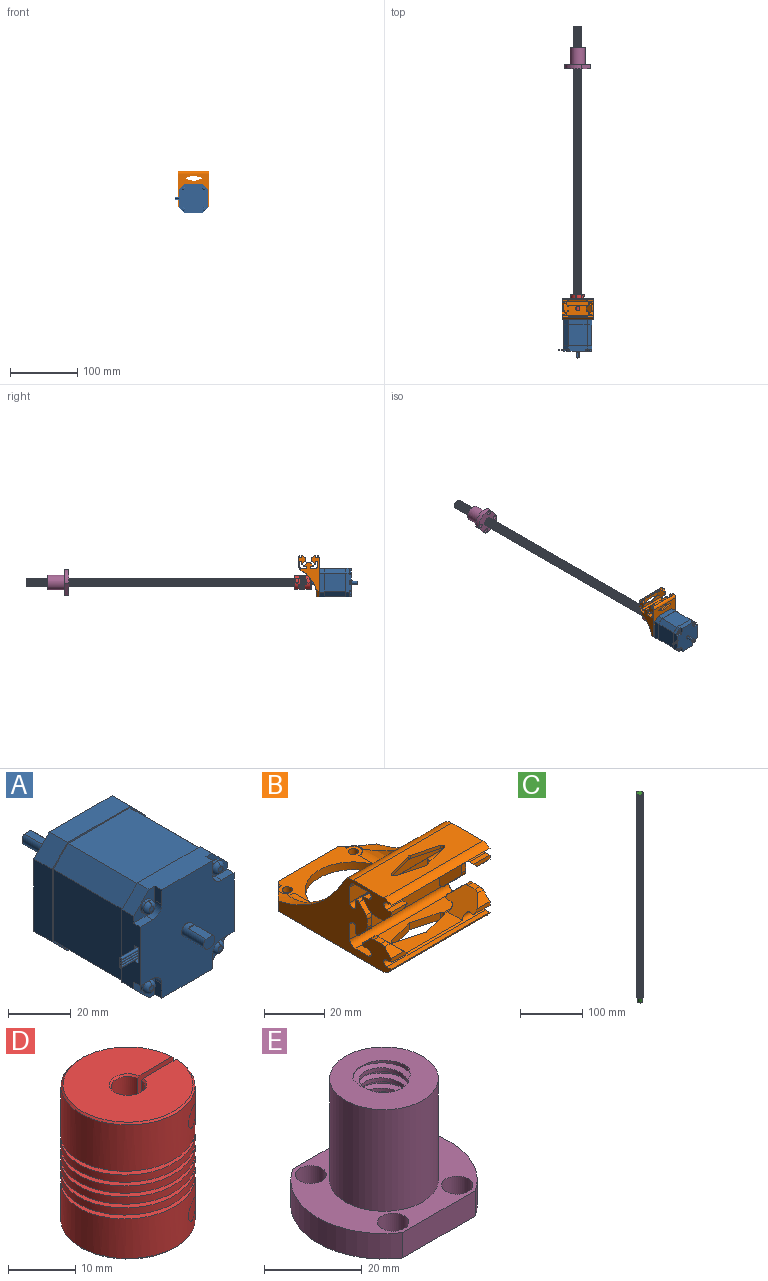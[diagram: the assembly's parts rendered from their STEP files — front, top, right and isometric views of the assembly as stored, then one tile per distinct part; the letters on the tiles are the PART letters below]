
ASSEMBLY  parts=5 mates=4
PART A: 93 faces, bbox 49.3x82x42.3 mm
  f0: plane 42.3x42.3mm, normal (0,1,0), area 858.8mm2, adj f1,f13,f15,f17,f19,f21,f32,f34
  f1: plane 8.25x7mm, normal (0.71,0,0.71), area 81.7mm2, adj f0,f3,f21,f34
  f2: plane 7x7mm, normal (0.71,0,0.71), area 52mm2, adj f12,f22,f23,f35
  f3: plane 42.3x42.3mm, normal (0,-1,0), area 75.6mm2, adj f1,f4,f5,f6,f7,f8,f9,f10
  f4: plane 31.5x6.71mm, normal (0.71,0,0.71), area 298.8mm2, adj f3,f5,f11,f12
  f5: plane 31.5x27.89mm, normal (1,0,0), area 878.4mm2, adj f3,f4,f6,f12
  f6: plane 31.5x6.71mm, normal (0.71,0,-0.71), area 298.8mm2, adj f3,f5,f7,f12
  f7: plane 31.5x27.89mm, normal (0,0,-1), area 878.4mm2, adj f3,f6,f8,f12
  f8: plane 31.5x6.71mm, normal (-0.71,0,-0.71), area 298.8mm2, adj f3,f7,f9,f12
  f9: plane 31.5x27.89mm, normal (-1,0,0), area 878.4mm2, adj f3,f8,f10,f12
  f10: plane 31.5x6.71mm, normal (-0.71,0,0.71), area 298.8mm2, adj f3,f9,f11,f12
  f11: plane 31.5x27.89mm, normal (0,0,1), area 878.4mm2, adj f3,f4,f10,f12
  f12: plane 42.3x42.3mm, normal (0,1,0), area 75.6mm2, adj f2,f4,f5,f6,f7,f8,f9,f10
  f13: plane 28.3x8.25mm, normal (-1,0,0), area 233.5mm2, adj f0,f3,f15,f32
  f14: plane 28.3x8.25mm, normal (-1,0,0), area 207.1mm2, adj f12,f16,f27,f29,f31,f33,f49,f50
  f15: plane 8.25x7mm, normal (-0.71,0,-0.71), area 81.7mm2, adj f0,f3,f13,f17
  f16: plane 7x7mm, normal (-0.71,0,-0.71), area 52mm2, adj f12,f14,f18,f49
  f17: plane 28.3x8.25mm, normal (0,0,-1), area 233.5mm2, adj f0,f3,f15,f19
  f18: plane 28.3x8.25mm, normal (0,0,-1), area 217.6mm2, adj f12,f16,f20,f27,f41,f42,f48,f49
  f19: plane 8.25x7mm, normal (0.71,0,-0.71), area 81.7mm2, adj f0,f3,f17,f21
  f20: plane 7x7mm, normal (0.71,0,-0.71), area 52mm2, adj f12,f18,f22,f41
  f21: plane 28.3x8.25mm, normal (1,0,0), area 233.5mm2, adj f0,f1,f3,f19
  f22: plane 28.3x8.25mm, normal (1,0,0), area 217.6mm2, adj f2,f12,f20,f23,f26,f27,f40,f41
  f23: plane 9.65x9.65mm, normal (0,-1,0), area 46.4mm2, adj f2,f22,f24,f25,f26,f35,f60
  f24: plane 5.65x3mm, normal (1,0,0), area 17mm2, adj f23,f25,f27,f35
  f25: cylinder r=4mm len=4mm, axis (0,1,0), area 18.8mm2, adj f23,f24,f26,f27
  f26: plane 5.65x3mm, normal (0,0,1), area 17mm2, adj f22,f23,f25,f27
  f27: plane 42.3x42.3mm, normal (0,-1,0), area 1410.9mm2, adj f14,f18,f22,f24,f25,f26,f28,f30
  f28: plane 5.65x3mm, normal (-1,0,0), area 17mm2, adj f27,f29,f30,f35
  f29: plane 9.65x9.65mm, normal (0,-1,0), area 46.4mm2, adj f14,f28,f30,f31,f33,f35,f36
  f30: cylinder r=4mm len=4mm, axis (0,-1,0), area 18.8mm2, adj f27,f28,f29,f31
  f31: plane 5.65x3mm, normal (0,0,1), area 17mm2, adj f14,f27,f29,f30
  f32: plane 8.25x7mm, normal (-0.71,0,0.71), area 81.7mm2, adj f0,f3,f13,f34
  f33: plane 7x7mm, normal (-0.71,0,0.71), area 52mm2, adj f12,f14,f29,f35
  f34: plane 28.3x8.25mm, normal (0,0,1), area 233.5mm2, adj f0,f1,f3,f32
  f35: plane 28.3x8.25mm, normal (0,0,1), area 217.6mm2, adj f2,f12,f23,f24,f27,f28,f29,f33
  f36: cylinder r=2.45mm len=4.9mm, axis (0,-1,0), area 15.4mm2, adj f29,f37,f39
  f37: torus R=0.95mm, axis (0,-1,0), area 14.1mm2, adj f36,f38,f39
  f38: plane 1.9x1.9mm, normal (0,-1,0), area 2.8mm2, adj f37,f39
  f39: torus R=0.95mm, axis (0,-1,0), area 14.1mm2, adj f36,f37,f38
  f40: plane 5.65x3mm, normal (0,0,-1), area 17mm2, adj f22,f27,f41,f43
  f41: plane 9.65x9.65mm, normal (0,-1,0), area 46.4mm2, adj f18,f20,f22,f40,f42,f43,f44
  f42: plane 5.65x3mm, normal (1,0,0), area 17mm2, adj f18,f27,f41,f43
  f43: cylinder r=4mm len=4mm, axis (0,-1,0), area 18.8mm2, adj f27,f40,f41,f42
  f44: cylinder r=2.45mm len=4.9mm, axis (0,-1,0), area 15.4mm2, adj f41,f45,f47
  f45: torus R=0.95mm, axis (0,-1,0), area 14.1mm2, adj f44,f46,f47
  f46: plane 1.9x1.9mm, normal (0,-1,0), area 2.8mm2, adj f45,f47
  f47: torus R=0.95mm, axis (0,-1,0), area 14.1mm2, adj f44,f45,f46
  f48: plane 5.65x3mm, normal (-1,0,0), area 17mm2, adj f18,f27,f49,f51
  f49: plane 9.65x9.65mm, normal (0,-1,0), area 46.4mm2, adj f14,f16,f18,f48,f50,f51,f52
  f50: plane 5.65x3mm, normal (0,0,-1), area 17mm2, adj f14,f27,f49,f51
  f51: cylinder r=4mm len=4mm, axis (0,1,0), area 18.8mm2, adj f27,f48,f49,f50
  f52: cylinder r=2.45mm len=4.9mm, axis (0,1,0), area 15.4mm2, adj f49,f53,f55
  f53: torus R=0.95mm, axis (0,1,0), area 14.1mm2, adj f52,f54,f55
  f54: plane 1.9x1.9mm, normal (0,-1,0), area 2.8mm2, adj f53,f55
  f55: torus R=0.95mm, axis (0,1,0), area 14.1mm2, adj f52,f53,f54
  f56: cylinder r=2.5mm len=10mm, axis (0,-1,0), area 131.3mm2, adj f27,f57,f58,f59
  f57: plane 8x3mm, normal (0,0,1), area 24mm2, adj f56,f58,f59
  f58: plane 5x4.5mm, normal (0,-1,0), area 18.6mm2, adj f56,f57
  f59: plane 3x0.5mm, normal (0,-1,0), area 1mm2, adj f56,f57
  f60: cylinder r=2.45mm len=4.9mm, axis (0,1,0), area 15.4mm2, adj f23,f61,f63
  f61: torus R=0.95mm, axis (0,1,0), area 14.1mm2, adj f60,f62,f63
  f62: plane 1.9x1.9mm, normal (0,-1,0), area 2.8mm2, adj f61,f63
  f63: torus R=0.95mm, axis (0,1,0), area 14.1mm2, adj f60,f61,f62
  f64: plane 3x1.75mm, normal (0,0,1), area 5.3mm2, adj f14,f65,f67,f68
  f65: plane 6x3mm, normal (0,-1,0), area 18mm2, adj f14,f64,f66,f68
  f66: plane 3x1.75mm, normal (0,0,-1), area 5.3mm2, adj f14,f65,f67,f68
  f67: plane 6x3mm, normal (0,1,0), area 18mm2, adj f14,f64,f66,f68
  f68: plane 6x1.75mm, normal (-1,0,0), area 7.6mm2, adj f64,f65,f66,f67,f69,f71,f73,f75
  f69: cylinder r=0.48mm len=10mm, axis (-1,0,0), area 30mm2, adj f68,f70
  f70: plane 0.96x0.96mm, normal (-1,0,0), area 0.7mm2, adj f69
  f71: cylinder r=0.48mm len=10mm, axis (-1,0,0), area 30mm2, adj f68,f72
  f72: plane 0.96x0.96mm, normal (-1,0,0), area 0.7mm2, adj f71
  f73: cylinder r=0.48mm len=10mm, axis (-1,0,0), area 30mm2, adj f68,f74
  f74: plane 0.96x0.96mm, normal (-1,0,0), area 0.7mm2, adj f73
  f75: cylinder r=0.48mm len=10mm, axis (-1,0,0), area 30mm2, adj f68,f76
  f76: plane 0.96x0.96mm, normal (-1,0,0), area 0.7mm2, adj f75
  f77: cylinder r=1.5mm len=4.5mm, axis (0,-1,0), area 42.4mm2, adj f0,f78
  f78: plane 3x3mm, normal (0,1,0), area 7.1mm2, adj f77
  f79: cylinder r=1.5mm len=4.5mm, axis (0,1,0), area 42.4mm2, adj f0,f80
  f80: plane 3x3mm, normal (0,1,0), area 7.1mm2, adj f79
  f81: cylinder r=1.5mm len=4.5mm, axis (0,1,0), area 42.4mm2, adj f0,f82
  f82: plane 3x3mm, normal (0,1,0), area 7.1mm2, adj f81
  f83: cylinder r=1.5mm len=4.5mm, axis (0,-1,0), area 42.4mm2, adj f0,f84
  f84: plane 3x3mm, normal (0,1,0), area 7.1mm2, adj f83
  f85: cylinder r=16mm len=32mm, axis (0,1,0), area 40.2mm2, adj f0,f86
  f86: plane 32x32mm, normal (0,1,0), area 424.1mm2, adj f85,f87
  f87: cylinder r=11mm len=22mm, axis (0,1,0), area 165.9mm2, adj f86,f88
  f88: plane 22x22mm, normal (0,1,0), area 360.5mm2, adj f87,f89
  f89: cylinder r=2.5mm len=22mm, axis (0,1,0), area 297.3mm2, adj f88,f90,f91,f92
  f90: plane 3x0.5mm, normal (0,1,0), area 1mm2, adj f89,f91
  f91: plane 15x3mm, normal (0,0,1), area 45mm2, adj f89,f90,f92
  f92: plane 5x4.5mm, normal (0,1,0), area 18.6mm2, adj f89,f91
PART B: 135 faces, bbox 47.1x62.8x30.9 mm
  f0: cylinder r=1.4mm len=11.38mm, axis (1,0,0), area 40.8mm2, adj f41,f57,f59,f110,f115,f127
  f1: cylinder r=1.4mm len=11.38mm, axis (1,0,0), area 40.8mm2, adj f41,f75,f77,f107,f114,f130
  f2: plane 7.5x1.61mm, normal (0,-1,0), area 10.7mm2, adj f41,f83,f84,f114
  f3: plane 7.5x1.61mm, normal (0,-1,0), area 10.7mm2, adj f41,f50,f51,f115
  f4: plane 7.5x2.03mm, normal (0,0,1), area 15.2mm2, adj f38,f43,f49,f111
  f5: plane 5.89x3.16mm, normal (0,-0.71,-0.71), area 19.3mm2, adj f6,f38,f43,f111
  f6: cylinder r=2.75mm len=2.73mm, axis (1,0,0), area 4.2mm2, adj f5,f7,f38,f111
  f7: plane 3.24x2.22mm, normal (0,0,-1), area 7.2mm2, adj f6,f8,f38,f111
  f8: cylinder r=2.75mm len=2.73mm, axis (1,0,0), area 4.2mm2, adj f7,f9,f38,f111
  f9: plane 6.06x3.33mm, normal (0,0.71,-0.71), area 20.7mm2, adj f8,f10,f38,f111
  f10: cylinder r=0.72mm len=7.5mm, axis (1,0,0), area 14.9mm2, adj f9,f11,f38,f111
  f11: plane 7.5x2.14mm, normal (0,0,1), area 16mm2, adj f10,f38,f58,f111
  f12: plane 7.2x2.13mm, normal (0,1,0), area 15.3mm2, adj f13,f38,f62,f112
  f13: cylinder r=0.72mm len=7.2mm, axis (1,0,0), area 14.3mm2, adj f12,f14,f38,f112
  f14: plane 5.76x3.33mm, normal (0,-0.71,0.71), area 19.3mm2, adj f13,f15,f38,f112
  f15: cylinder r=2.75mm len=2.43mm, axis (1,0,0), area 3.6mm2, adj f14,f16,f38,f108,f112
  f16: plane 3.24x2mm, normal (0,-1,0), area 6.5mm2, adj f15,f17,f38,f108
  f17: cylinder r=2.75mm len=3.09mm, axis (1,0,0), area 6.3mm2, adj f16,f18,f38,f108,f112
  f18: plane 5.76x2.67mm, normal (0,-0.71,-0.71), area 16.7mm2, adj f17,f19,f38,f112
  f19: cylinder r=0.72mm len=7.2mm, axis (1,0,0), area 14.3mm2, adj f18,f20,f38,f112
  f20: plane 7.2x2.13mm, normal (0,1,0), area 15.3mm2, adj f19,f21,f38,f112
  f21: cylinder r=1.4mm len=10mm, axis (1,0,0), area 37.8mm2, adj f20,f38,f73,f112
  f22: plane 7.5x2.13mm, normal (0,0,-1), area 16mm2, adj f23,f38,f76,f113
  f23: cylinder r=0.72mm len=7.5mm, axis (1,0,0), area 14.9mm2, adj f22,f24,f38,f113
  f24: plane 6.06x3.33mm, normal (0,0.71,0.71), area 20.7mm2, adj f23,f25,f38,f113
  f25: cylinder r=2.75mm len=2.73mm, axis (1,0,0), area 4.2mm2, adj f24,f26,f38,f113
  f26: plane 3.24x2.22mm, normal (0,0,1), area 7.2mm2, adj f25,f27,f38,f113
  f27: cylinder r=2.75mm len=2.73mm, axis (1,0,0), area 4.2mm2, adj f26,f28,f38,f113
  f28: plane 5.89x3.16mm, normal (0,-0.71,0.71), area 19.3mm2, adj f27,f38,f42,f113
  f29: plane 7.5x2.03mm, normal (0,0,-1), area 15.2mm2, adj f38,f42,f85,f113
  f30: cylinder r=1.7mm len=3.4mm, axis (0,0,-1), area 33.9mm2, adj f37,f46
  f31: cylinder r=1.7mm len=3.4mm, axis (0,0,-1), area 33.9mm2, adj f34,f46
  f32: cylinder r=1.7mm len=3.4mm, axis (0,0,-1), area 33.9mm2, adj f40,f46
  f33: cylinder r=1.7mm len=3.4mm, axis (0,0,-1), area 33.9mm2, adj f40,f46
  f34: plane 13.35x12.54mm, normal (0,0,1), area 46.3mm2, adj f31,f35,f45,f98,f103
  f35: cylinder r=6mm len=28.38mm, axis (0,1,0), area 205.2mm2, adj f34,f40,f45,f87,f90,f99,f103,f105
  f36: cylinder r=6mm len=1.74mm, axis (0,-1,0), area 1.1mm2, adj f40,f89,f106,f133
  f37: plane 13.35x12.54mm, normal (0,0,1), area 46.3mm2, adj f30,f45,f91,f96,f104
  f38: plane 53x30.18mm, normal (1,0,0), area 754.6mm2, adj f4,f5,f6,f7,f8,f9,f10,f11
  f39: plane 30.3x21.02mm, normal (0,1,0), area 601.9mm2, adj f92,f94,f96,f97,f98,f100,f117
  f40: plane 37x16mm, normal (0,0,1), area 257.9mm2, adj f32,f33,f35,f36,f44,f45,f91,f93
  f41: plane 53x30.18mm, normal (-1,0,0), area 754.6mm2, adj f0,f1,f2,f3,f46,f47,f48,f49
  f42: plane 7.5x1.61mm, normal (0,-1,0), area 10.7mm2, adj f28,f29,f38,f113
  f43: plane 7.5x1.61mm, normal (0,-1,0), area 10.7mm2, adj f4,f5,f38,f111
  f44: plane 28.3x3.18mm, normal (0,1,0), area 89.9mm2, adj f40,f46,f133,f134
  f45: cylinder r=16mm len=32mm, axis (0,0,-1), area 319.2mm2, adj f34,f35,f37,f40,f46,f91,f97
  f46: plane 57.47x46.3mm, normal (0,0,-1), area 1624.3mm2, adj f30,f31,f32,f33,f38,f41,f44,f45
  f47: plane 46.3x14.48mm, normal (0,0,1), area 555.3mm2, adj f38,f41,f100,f101,f118,f119,f120,f121
  f48: plane 46.3x2.03mm, normal (0,0,-1), area 93.8mm2, adj f38,f41,f49,f101
  f49: cylinder r=1.4mm len=46.3mm, axis (1,0,0), area 103.6mm2, adj f4,f38,f41,f48,f50,f110,f111,f115
  f50: plane 7.5x2.03mm, normal (0,0,1), area 15.2mm2, adj f3,f41,f49,f115
  f51: plane 5.89x3.16mm, normal (0,-0.71,-0.71), area 19.3mm2, adj f3,f41,f52,f115
  f52: cylinder r=2.75mm len=2.73mm, axis (1,0,0), area 4.2mm2, adj f41,f51,f53,f115
  f53: plane 3.24x2.22mm, normal (0,0,-1), area 7.2mm2, adj f41,f52,f54,f115
  f54: cylinder r=2.75mm len=2.73mm, axis (1,0,0), area 4.2mm2, adj f41,f53,f55,f115
  f55: plane 6.06x3.33mm, normal (0,0.71,-0.71), area 20.7mm2, adj f41,f54,f56,f115
  f56: cylinder r=0.72mm len=7.5mm, axis (1,0,0), area 14.9mm2, adj f41,f55,f57,f115
  f57: plane 7.5x2.14mm, normal (0,0,1), area 16mm2, adj f0,f41,f56,f115
  f58: cylinder r=1.4mm len=11.38mm, axis (1,0,0), area 40.8mm2, adj f11,f38,f59,f110,f111,f128
  f59: plane 46.3x6.22mm, normal (0,0,-1), area 233.1mm2, adj f0,f38,f41,f58,f60,f120,f121,f126
  f60: cylinder r=2.4mm len=46.3mm, axis (1,0,0), area 177.1mm2, adj f38,f41,f59,f61
  f61: plane 46.3x6.22mm, normal (0,-1,0), area 288.1mm2, adj f38,f41,f60,f62
  f62: cylinder r=1.4mm len=46.3mm, axis (1,0,0), area 77.7mm2, adj f12,f38,f41,f61,f63,f73,f112,f116
  f63: plane 7.2x2.13mm, normal (0,1,0), area 15.3mm2, adj f41,f62,f64,f116
  f64: cylinder r=0.72mm len=7.2mm, axis (1,0,0), area 14.3mm2, adj f41,f63,f65,f116
  f65: plane 5.76x3.33mm, normal (0,-0.71,0.71), area 19.3mm2, adj f41,f64,f66,f116
  f66: cylinder r=2.75mm len=2.43mm, axis (1,0,0), area 3.6mm2, adj f41,f65,f67,f109,f116
  f67: plane 3.24x2mm, normal (0,-1,0), area 6.5mm2, adj f41,f66,f68,f109
  f68: cylinder r=2.75mm len=3.09mm, axis (1,0,0), area 6.3mm2, adj f41,f67,f69,f109,f116
  f69: plane 5.76x2.67mm, normal (0,-0.71,-0.71), area 16.7mm2, adj f41,f68,f70,f116
  f70: cylinder r=0.72mm len=7.2mm, axis (1,0,0), area 14.3mm2, adj f41,f69,f71,f116
  f71: plane 7.2x2.13mm, normal (0,1,0), area 15.3mm2, adj f41,f70,f72,f116
  f72: cylinder r=1.4mm len=10mm, axis (1,0,0), area 37.8mm2, adj f41,f71,f73,f116
  f73: plane 46.3x14.87mm, normal (0,-1,0), area 483.8mm2, adj f21,f38,f41,f62,f72,f74,f112,f116
  f74: cylinder r=2.4mm len=46.3mm, axis (1,0,0), area 177.1mm2, adj f38,f41,f73,f75
  f75: plane 46.3x6.22mm, normal (0,0,1), area 233.1mm2, adj f1,f38,f41,f74,f76,f122,f123,f130
  f76: cylinder r=1.4mm len=11.38mm, axis (1,0,0), area 40.8mm2, adj f22,f38,f75,f107,f113,f132
  f77: plane 7.5x2.13mm, normal (0,0,-1), area 16mm2, adj f1,f41,f78,f114
  f78: cylinder r=0.72mm len=7.5mm, axis (1,0,0), area 14.9mm2, adj f41,f77,f79,f114
  f79: plane 6.06x3.33mm, normal (0,0.71,0.71), area 20.7mm2, adj f41,f78,f80,f114
  f80: cylinder r=2.75mm len=2.73mm, axis (1,0,0), area 4.2mm2, adj f41,f79,f81,f114
  f81: plane 3.24x2.22mm, normal (0,0,1), area 7.2mm2, adj f41,f80,f82,f114
  f82: cylinder r=2.75mm len=2.73mm, axis (1,0,0), area 4.2mm2, adj f41,f81,f83,f114
  f83: plane 5.89x3.16mm, normal (0,-0.71,0.71), area 19.3mm2, adj f2,f41,f82,f114
  f84: plane 7.5x2.03mm, normal (0,0,-1), area 15.2mm2, adj f2,f41,f85,f114
  f85: cylinder r=1.4mm len=46.3mm, axis (1,0,0), area 103.6mm2, adj f29,f38,f41,f84,f86,f107,f113,f114
  f86: plane 46.3x2.03mm, normal (0,0,1), area 93.8mm2, adj f38,f41,f85,f102
  f87: plane 12.79x11.02mm, normal (1,0,0), area 61.5mm2, adj f35,f90,f94
  f88: plane 12.79x11.02mm, normal (-1,0,0), area 61.5mm2, adj f89,f91,f92
  f89: cylinder r=45mm len=38.01mm, axis (1,0,0), area 113.1mm2, adj f36,f38,f88,f91,f92,f100,f106,f133
  f90: cylinder r=45mm len=38.01mm, axis (1,0,0), area 113.1mm2, adj f35,f41,f87,f93,f94,f100,f105,f134
  f91: cylinder r=6mm len=28.38mm, axis (0,-1,0), area 205.2mm2, adj f37,f40,f45,f88,f89,f95,f104,f106
  f92: cylinder r=6mm len=20.88mm, axis (0,0,-1), area 160.6mm2, adj f39,f88,f89,f95,f100
  f93: cylinder r=6mm len=1.74mm, axis (0,1,0), area 1.1mm2, adj f40,f90,f105,f134
  f94: cylinder r=6mm len=20.88mm, axis (0,0,1), area 160.6mm2, adj f39,f87,f90,f99,f100
  f95: bspline ~7.42x6mm, area 34.4mm2, adj f91,f92,f96,f104
  f96: cylinder r=5mm len=9.19mm, axis (-1,0,0), area 67mm2, adj f37,f39,f95,f97,f104
  f97: bspline ~14.98x5.95mm, area 84.3mm2, adj f39,f45,f96,f98
  f98: cylinder r=5mm len=9.19mm, axis (-1,0,0), area 67mm2, adj f34,f39,f97,f99,f103
  f99: bspline ~6.36x6mm, area 34.4mm2, adj f35,f94,f98,f103
  f100: cylinder r=5mm len=46.3mm, axis (1,0,0), area 183.2mm2, adj f38,f39,f41,f47,f89,f90,f92,f94
  f101: cylinder r=5mm len=46.3mm, axis (-1,0,0), area 171.1mm2, adj f38,f41,f47,f48
  f102: cylinder r=5mm len=46.3mm, axis (-1,0,0), area 262.3mm2, adj f38,f41,f46,f86
  f103: cylinder r=3mm len=6mm, axis (0,0,1), area 13.3mm2, adj f34,f35,f98,f99
  f104: cylinder r=3mm len=6mm, axis (0,0,1), area 13.3mm2, adj f37,f91,f95,f96
  f105: cylinder r=3mm len=6mm, axis (0,0,1), area 3.3mm2, adj f35,f40,f90,f93
  f106: cylinder r=3mm len=6mm, axis (0,0,1), area 3.3mm2, adj f36,f40,f89,f91
  f107: plane 26.3x6.97mm, normal (0,0,1), area 143.8mm2, adj f1,f76,f85,f113,f114,f124,f125,f130
  f108: plane 4.5x0.07mm, normal (-1,0,0), area 0.3mm2, adj f15,f16,f17,f112
  f109: plane 4.5x0.07mm, normal (1,0,0), area 0.3mm2, adj f66,f67,f68,f116
  f110: plane 26.3x6.97mm, normal (0,0,-1), area 143.8mm2, adj f0,f49,f58,f111,f115,f118,f119,f127
  f111: plane 14.33x8.54mm, normal (-0.71,0,-0.71), area 99.5mm2, adj f4,f5,f6,f7,f8,f9,f10,f11
  f112: plane 15.01x8.62mm, normal (-0.71,-0.71,0), area 103.6mm2, adj f12,f13,f14,f15,f17,f18,f19,f20
  f113: plane 14.33x8.54mm, normal (-0.71,0,0.71), area 99.5mm2, adj f22,f23,f24,f25,f26,f27,f28,f29
  f114: plane 14.33x8.54mm, normal (0.71,0,0.71), area 99.5mm2, adj f1,f2,f77,f78,f79,f80,f81,f82
  f115: plane 14.33x8.54mm, normal (0.71,0,-0.71), area 99.5mm2, adj f0,f3,f49,f50,f51,f52,f53,f54
  f116: plane 15.01x8.62mm, normal (0.71,-0.71,0), area 103.6mm2, adj f62,f63,f64,f65,f66,f68,f69,f70
  f117: cylinder r=3.17mm len=6.35mm, axis (0,1,0), area 32.6mm2, adj f39,f73
  f118: plane 11.12x2.97mm, normal (-0.26,0.97,0), area 18.4mm2, adj f47,f110,f128,f129
  f119: plane 11.12x2.97mm, normal (0.26,0.97,0), area 18.4mm2, adj f47,f110,f127,f129
  f120: plane 11.12x2.97mm, normal (0.26,-0.97,0), area 15mm2, adj f47,f59,f126,f127
  f121: plane 11.12x2.97mm, normal (-0.26,-0.97,0), area 15mm2, adj f47,f59,f126,f128
  f122: plane 11.38x3.03mm, normal (-0.26,-0.97,0), area 33.9mm2, adj f46,f75,f123,f132
  f123: plane 11.38x3.03mm, normal (0.26,-0.97,0), area 33.9mm2, adj f46,f75,f122,f130
  f124: plane 11.12x3.18mm, normal (0.26,0.97,0), area 36.5mm2, adj f46,f107,f130,f131
  f125: plane 11.12x3.18mm, normal (-0.26,0.97,0), area 36.5mm2, adj f46,f107,f131,f132
  f126: cylinder r=1mm len=1.31mm, axis (0,0,-1), area 0.7mm2, adj f47,f59,f120,f121
  f127: cylinder r=1mm len=1.93mm, axis (0,0,-1), area 3.7mm2, adj f0,f47,f59,f110,f119,f120
  f128: cylinder r=1mm len=1.93mm, axis (0,0,-1), area 3.7mm2, adj f47,f58,f59,f110,f118,f121
  f129: cylinder r=1mm len=1.6mm, axis (0,0,-1), area 0.8mm2, adj f47,f110,f118,f119
  f130: cylinder r=1mm len=3.18mm, axis (0,0,-1), area 7.8mm2, adj f1,f46,f75,f107,f123,f124
  f131: cylinder r=1mm len=3.18mm, axis (0,0,-1), area 1.7mm2, adj f46,f107,f124,f125
  f132: cylinder r=1mm len=3.18mm, axis (0,0,-1), area 7.8mm2, adj f46,f75,f76,f107,f122,f125
  f133: plane 9.04x9.04mm, normal (0.71,0.71,0), area 44.5mm2, adj f36,f38,f40,f44,f46,f89
  f134: plane 9.04x9.04mm, normal (-0.71,0.71,0), area 44.5mm2, adj f40,f41,f44,f46,f90,f93
PART C: 10 faces, bbox 12.7x14.7x410.4 mm
  f0: cylinder r=6.35mm len=400.05mm, axis (0,0,-1), area -4638.8mm2, adj f1,f2,f5,f7,f8,f9
  f1: plane 12.7x12.28mm, normal (0,0,-1), area 64.9mm2, adj f0,f3,f5,f6,f7
  f2: plane 12.7x12.29mm, normal (0,0,1), area 115.2mm2, adj f0,f6,f8,f9
  f3: cylinder r=4mm len=10mm, axis (0,0,1), area 251.3mm2, adj f1,f4
  f4: plane 8x8mm, normal (0,0,-1), area 50.3mm2, adj f3
  f5: plane 1.27x0.8mm, normal (0,-1,0), area 0.8mm2, adj f0,f1,f6,f9
  f6: cylinder r=5.08mm len=400.05mm, axis (0,0,1), area 12611.1mm2, adj f1,f2,f5,f7,f8,f9
  f7: bspline ~399.96x14.66mm, area 7450.8mm2, adj f0,f1,f6,f8
  f8: plane 1.27x0.8mm, normal (0,-1,0), area 0.8mm2, adj f0,f2,f6,f7
  f9: bspline ~399.96x14.66mm, area 7483.9mm2, adj f0,f2,f5,f6
PART D: 32 faces, bbox 24.4x23.3x26.3 mm
  f0: cone r=4mm half-angle=45deg, axis (0,0,-1), area 10.7mm2, adj f1,f2,f3,f4
  f1: plane 9.63x7.31mm, normal (0,-1,0), area 42.2mm2, adj f0,f2,f4,f5,f6,f7,f8
  f2: plane 19.4x19.39mm, normal (0,0,-1), area 232.6mm2, adj f0,f1,f3,f5
  f3: plane 9.58x7.31mm, normal (0,1,0), area 41.9mm2, adj f0,f2,f4,f5,f6,f9,f10
  f4: cylinder r=4mm len=12.2mm, axis (0,0,-1), area 244.1mm2, adj f0,f1,f3,f7,f8,f9,f10,f11
  f5: cone r=10mm half-angle=45deg, axis (0,0,1), area 25.9mm2, adj f1,f2,f3,f6
  f6: cylinder r=10mm len=24.4mm, axis (0,0,1), area 1299.1mm2, adj f1,f3,f5,f7,f10,f11,f12,f14
  f7: bspline ~23.13x22mm, area 1185.7mm2, adj f1,f4,f6,f13,f18,f19
  f8: cylinder r=1.7mm len=5.75mm, axis (0,1,0), area 57.2mm2, adj f1,f4,f20
  f9: cylinder r=1.7mm len=8.99mm, axis (0,1,0), area 82.2mm2, adj f3,f4,f21
  f10: bspline ~23.13x22mm, area 195mm2, adj f3,f4,f6,f11
  f11: plane 6x0.7mm, normal (-1,0,0), area 4.2mm2, adj f4,f6,f10,f12
  f12: bspline ~23.13x22mm, area 1319.3mm2, adj f4,f6,f11,f13,f14,f19
  f13: plane 8x7.24mm, normal (0,0,-1), area 19.9mm2, adj f4,f7,f12,f19
  f14: plane 8.92x8.39mm, normal (0,1,0), area 51.3mm2, adj f6,f12,f15,f19,f22,f23,f24
  f15: cone r=9.7mm half-angle=45deg, axis (0,0,-1), area 25.9mm2, adj f6,f14,f16,f23
  f16: plane 8.85x8.39mm, normal (0,-1,0), area 50.9mm2, adj f6,f15,f17,f19,f22,f23,f25
  f17: bspline ~14.4x11.57mm, area 69.1mm2, adj f6,f16,f18,f19
  f18: plane 7.5x0.7mm, normal (1,0,0), area 5.2mm2, adj f6,f7,f17,f19
  f19: cylinder r=2.5mm len=12.2mm, axis (0,0,1), area 159.1mm2, adj f7,f12,f13,f14,f16,f17,f18,f22
  f20: plane 6x5.85mm, normal (0,1,0), area 19mm2, adj f8,f26,f27
  f21: cylinder r=10mm len=3.4mm, axis (0,0,1), area 10.5mm2, adj f9
  f22: cone r=2.5mm half-angle=45deg, axis (0,0,1), area 6.7mm2, adj f14,f16,f19,f23
  f23: plane 19.4x19.39mm, normal (0,0,1), area 264.7mm2, adj f14,f15,f16,f22
  f24: cylinder r=1.7mm len=8.21mm, axis (0,1,0), area 83.7mm2, adj f14,f28
  f25: cylinder r=1.7mm len=5.75mm, axis (0,1,0), area 61.4mm2, adj f16,f29
  f26: cylinder r=10mm len=6mm, axis (0,0,1), area 30.3mm2, adj f20,f27
  f27: cylinder r=3mm len=6mm, axis (0,1,0), area 32.4mm2, adj f20,f26
  f28: cylinder r=10mm len=3.4mm, axis (0,0,1), area 10.5mm2, adj f24
  f29: plane 6x5.85mm, normal (0,1,0), area 19mm2, adj f25,f30,f31
  f30: cylinder r=10mm len=6mm, axis (0,0,1), area 30.3mm2, adj f29,f31
  f31: cylinder r=3mm len=6mm, axis (0,1,0), area 32.4mm2, adj f29,f30
PART E: 29 faces, bbox 38.4x32.1x32.8 mm
  f0: bspline ~31.23x14.66mm, area 563.7mm2, adj f2,f14,f15,f16,f17,f18,f19,f20
  f1: bspline ~30.39x14.66mm, area 539.1mm2, adj f2,f14,f15,f16,f17,f18,f19,f20
  f2: cylinder r=5.08mm len=30.15mm, axis (0,0,-1), area 304.8mm2, adj f0,f1,f14,f28
  f3: cylinder r=19.05mm len=31.75mm, axis (0,0,-1), area 238.3mm2, adj f4,f10,f11,f12
  f4: plane 21.06x6.35mm, normal (0,1,0), area 133.7mm2, adj f3,f5,f11,f12
  f5: cylinder r=19.05mm len=31.75mm, axis (0,0,-1), area 238.3mm2, adj f4,f10,f11,f12
  f6: cylinder r=3.17mm len=6.35mm, axis (0,0,-1), area 126.7mm2, adj f11,f12
  f7: cylinder r=3.17mm len=6.35mm, axis (0,0,-1), area 126.7mm2, adj f11,f12
  f8: cylinder r=3.17mm len=6.35mm, axis (0,0,-1), area 126.7mm2, adj f11,f12
  f9: cylinder r=3.17mm len=6.35mm, axis (0,0,-1), area 126.7mm2, adj f11,f12
  f10: plane 21.06x6.35mm, normal (0,-1,0), area 133.7mm2, adj f3,f5,f11,f12
  f11: plane 38.1x31.75mm, normal (0,0,1), area 534.7mm2, adj f3,f4,f5,f6,f7,f8,f9,f10
  f12: plane 38.1x31.75mm, normal (0,0,-1), area 796mm2, adj f3,f4,f5,f6,f7,f8,f9,f10
  f13: cylinder r=11.11mm len=25.4mm, axis (0,0,-1), area 1773.5mm2, adj f11,f14
  f14: plane 22.54x22.54mm, normal (0,0,1), area 284.3mm2, adj f0,f1,f2,f13,f27
  f15: cylinder r=6.35mm len=12.7mm, axis (0,0,1), area 37.7mm2, adj f0,f1,f16,f27
  f16: cylinder r=6.35mm len=12.7mm, axis (0,0,1), area 37.6mm2, adj f0,f1,f15,f17
  f17: cylinder r=6.35mm len=12.7mm, axis (0,0,1), area 37.6mm2, adj f0,f1,f16,f18
  f18: cylinder r=6.35mm len=12.7mm, axis (0,0,1), area 37.7mm2, adj f0,f1,f17,f19
  f19: cylinder r=6.35mm len=12.7mm, axis (0,0,1), area 37.6mm2, adj f0,f1,f18,f20
  f20: cylinder r=6.35mm len=12.7mm, axis (0,0,1), area 37.7mm2, adj f0,f1,f19,f21
  f21: cylinder r=6.35mm len=12.7mm, axis (0,0,1), area 37.7mm2, adj f0,f1,f20,f22
  f22: cylinder r=6.35mm len=12.7mm, axis (0,0,1), area 37.6mm2, adj f0,f1,f21,f23
  f23: cylinder r=6.35mm len=12.7mm, axis (0,0,1), area 37.7mm2, adj f0,f1,f22,f24
  f24: cylinder r=6.35mm len=12.7mm, axis (0,0,1), area 37.7mm2, adj f0,f1,f23,f25
  f25: cylinder r=6.35mm len=12.7mm, axis (0,0,1), area 37.6mm2, adj f0,f1,f24,f26
  f26: cylinder r=6.35mm len=12.7mm, axis (0,0,1), area 101.4mm2, adj f0,f12,f25,f28
  f27: cylinder r=6.35mm len=10.78mm, axis (0,0,1), area 7mm2, adj f1,f14,f15
  f28: plane 1.6x1.27mm, normal (0,-1,0), area 1.6mm2, adj f0,f1,f2,f26
PLACE A t=(45.85,-450.85,25.85)mm fixed
PLACE B rot(axis=(-1,0,0),90deg) t=(45.85,-450.85,25.85)mm
PLACE C rot(axis=(-0.1,0.7,0.7),168.4deg) t=(45.81,-413.85,25.99)mm
PLACE D rot(axis=(0.47,-0.63,0.63),129.9deg) t=(45.81,-438.85,25.99)mm
PLACE E rot(axis=(-0.32,-0.67,-0.67),144.7deg) t=(45.81,-77.77,25.99)mm
MATE revolute D.f23 <-> A.f56  axis (0,-1,0) through (45.85,-438.85,25.85)mm
MATE fastened D.f0 <-> C.f3  axis (0,1,0) through (45.81,-413.85,25.99)mm
MATE cylindrical E.f2 <-> C.f0  axis (0,-1,0) through (45.81,-77.77,25.99)mm
MATE fastened B.f45 <-> A.f56  axis (0,-1,0) through (45.85,-450.85,25.85)mm
